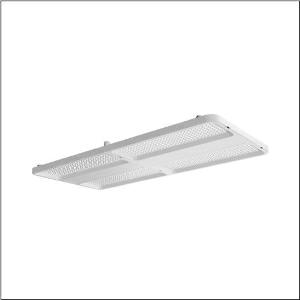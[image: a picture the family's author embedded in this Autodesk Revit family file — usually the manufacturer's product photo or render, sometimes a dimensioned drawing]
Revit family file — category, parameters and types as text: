
# Revit family: highbay_21_maxi_52hn11db4qea
name_source: partatom
category: Lighting Fixtures
units: mm (PartAtom-declared; Revit-internal decimal feet)

## family parameters
Cut with Voids When Loaded = No
Host = Face
Light Source = No
Part Type = Normal
Room Calculation Point = No
Round Connector Dimension = Use Diameter
Shared = No

## types (1)
- --- (1 x LED, 5840 lm, 31.4 W, 4000K)
    Apparent Load = 31 VA
    CIE Flux Codes = 89 97 99 100 100
    Color Rendering = 80
    Color Temperature = 4000K
    Default Elevation = 1800 mm
    Description = high bay luminaire Highbay 21 maxi; direct symmetric narrow distribution, light control with lens of PMMA; UGR ≤ 22 (X = 4H | Y = 8H | S = 0.25H | reflection values 70/50/20); luminous flux: 38.000lm; light colour: 840, colour temperature: 4000K, MacAdam ≤ 3 SDCM (initial), colour rendering: CRI > 80; luminous efficacy: 192,2lm/W; rated service life: 75.000h (L80) at AT= ta max; control: DALI 2; luminaire connection: 2x terminal, 5-pole, max. 2.5mm² with through-wiring: 1x feed-in / 1x feed-out (cable entry for two cables, Ø 8.5..13mm); mains connection: 230..240V, AC/DC 0/50..60Hz; connected load: 197,7W; protection rating (complete): IP66; insulation class (complete): insulation class I (protective earthing); protection symbol: D; impact resistance: IK08; certification: CE, ENEC, VDE, UKCA; luminaire for central battery installations according to EN 60598-2-22, internal wiring halogen-free; luminaire LABS conformity tested according to VDMA 24364:2018-05; Suitable for use in the food industry according to the specifications of IFS-Food, HACCP and/or BRC; housing frame of high-performance plastic PA6, matt traffic white (RAL 9016); cover of PMMA; dimension (LxWxH): 946 x 442 x 72mm; permissible operating ambient temperature: -40..+60°C (reducing of maximum allowable ambient temperature of 5°C with ceiling mounting); packaging unit: 1 piece; (delivery without accessories; please order mounting accessories separately)
    Height = 72 mm  [stored 0.23622 ft]
    Lamp = 1 x LED
    Lamp Light Flux = 5840 lm
    Lamp Power = 31.4 W
    Lamp count = 1
    Length = 946 mm
    Luminous efficacy = 186 lm/W
    Manufacturer = Siteco
    ModVariant = No
    Model = 52HN11DB4QEA
    Mounting Place = Ceiling
    Mounting Type = Pendant
    Number of Poles = 1
    OnlyDefault = Yes
    Power Factor = 1
    Product Name = Highbay 21 maxi
    Product group = high bay luminaire
    ProductGroupID = 902
    Protection Class = Protection class I
    Protection Degree = IP 66
    RLX_Detail_Level = 1
    RLX_Emergency_Light_Flux = 0 lm
    RLX_Emergency_Type = 0
    RLX_Emergency_Type_DB = No
    RlxData = <blob elided: 127925 chars, md5=326277ce>
    Socket = socket
    Standby Power = 0 W
    System Light Flux = 5840 lm
    System Power = 31 W
    Type Comments = : DC mode (central or group accumulator) initial emergency light level
    Type Image = l_1363244.jpg
    URL = http://relux.com
    VarID = @adj_017769
    Voltage = 0 V
    Weight = 0.00 kg
    Width = 442 mm

note: [stored X ft] marks values corroborated as IEEE doubles in the binary element streams (Revit-internal decimal feet)

## geometry (parser evidence)
native form markers: Blend x4, Sweep x10
no freeform markers — native parametric forms only
